# Revit family: KM4 Pole Mount
name_source: partatom
category: Lighting Fixtures
revit_build: Autodesk Revit 2013 (Build: 20120221_2030(x64)
units: mm (PartAtom-declared; Revit-internal decimal feet)

## types (4) — shared parameters
Apparent Load = 24 VA
Assembly Code = D5020280
Default Elevation = 48 "
Description = KM4 is the most compact version of KicK and is ideal for even the most discrete architectural applications
Finish = Hubbell-Titanium
Glass = Hubbell-Glass
Lamp = LED
Load Classification = Lighting
Manufacturer = Architectural Area Lighting
Manufacturer Fax = 626-369-2695
Model = KicK™ Mini Small
Photometrics Web = Web K4 : KM4-T4-2050
Power Factor = 1
Product Documentation Link = http://www.aal.net
Product Page URL = http://www.aal.net
URL = http://www.aal.net
Voltage = 120 V
Watts = 24 W

## per-type parameters (varying)
| type | Lamp-1 | Lamp-2 | Lamp-3 | Lamp-4 | Model Type |
| KM41 | Yes | No | No | No | Single fixture |
| KM42 | No | Yes | No | Yes | Two fixtures 180º apart |
| KM43 | Yes | Yes | No | Yes | Three fixtures 90º apart |
| KM44 | Yes | Yes | Yes | Yes | Four fixtures 90º apart |

## geometry (parser evidence)
native form markers: Blend x40, Sweep x7
no freeform markers — native parametric forms only
